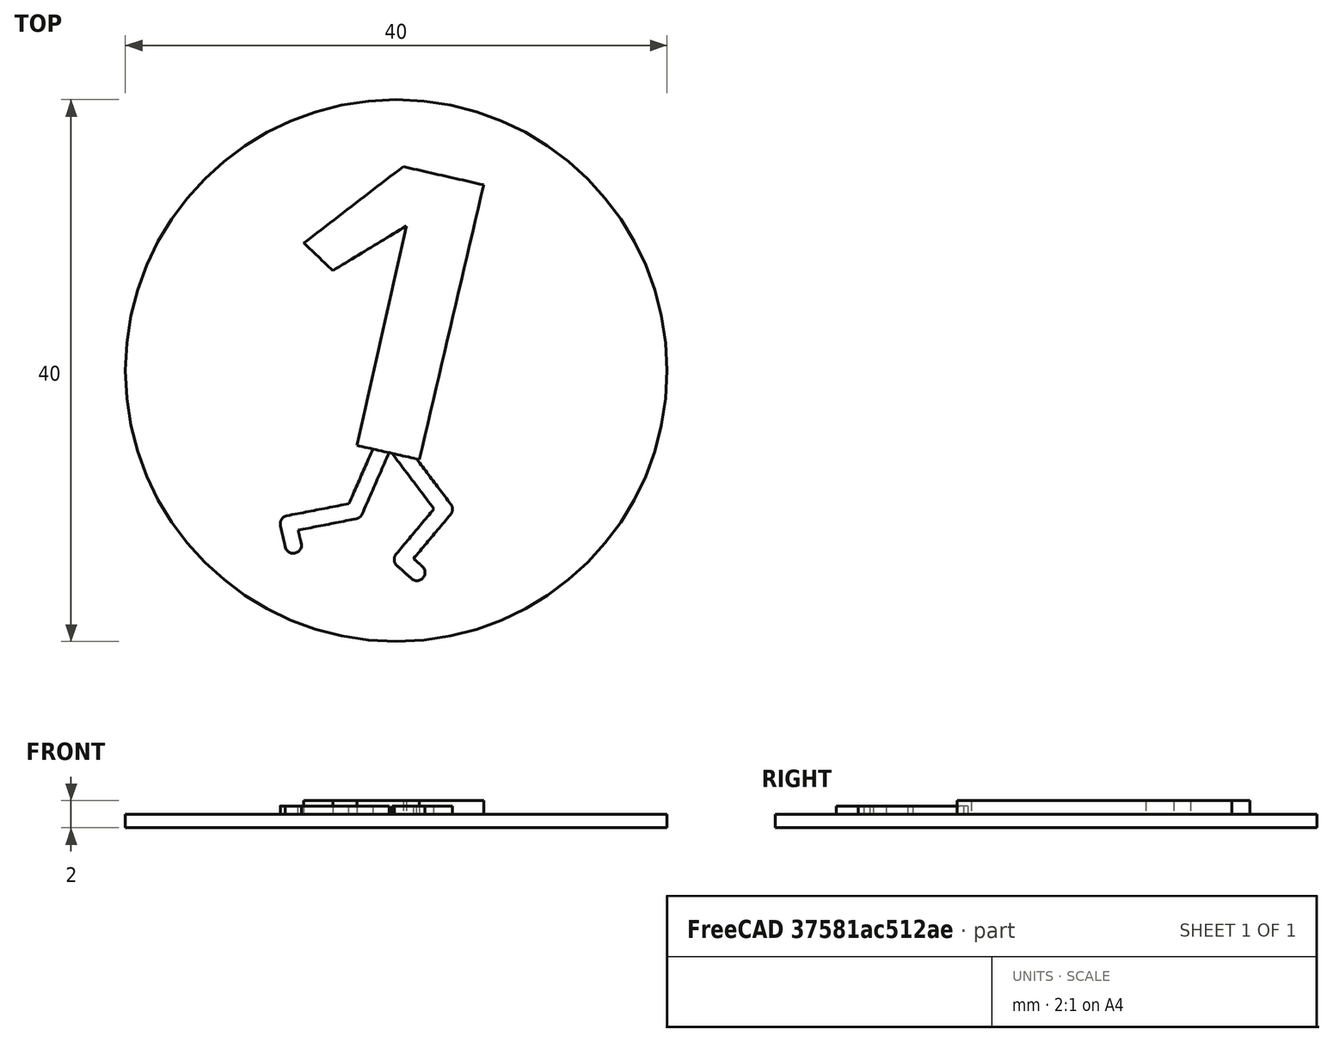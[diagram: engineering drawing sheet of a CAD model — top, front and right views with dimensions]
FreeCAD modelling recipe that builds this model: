
FCSTD DOCUMENT  (FreeCAD 0.17R12412 (Git))
Label: Bit-1-moneda
License: All rights reserved
LicenseURL: http://en.wikipedia.org/wiki/All_rights_reserved
objects: Part::Feature×2, Part::Extrusion×2, Part::MultiFuse×2, Part::Cylinder×1
note: 7 computed .brp shape members not serialized (recipe doc carries the construction recipe); baked Part::Feature solids carry a one-line shape summary decoded from their .brp

FEATURE [Part::Feature] path4_7_6_1_6
  Placement = pos=(-19.6018,20.3411,1) rot=(0,0,1;0rad)
  shape: bbox 13.27 x 21.62 x 2e-07 mm, 0 faces, 0 solids (baked)
FEATURE [Part::Feature] path6_7_2_1_0_9
  Placement = pos=(-19.6018,20.3411,1) rot=(0,0,1;0rad)
  shape: bbox 12.78 x 10.69 x 2e-07 mm, 0 faces, 0 solids (baked)
FEATURE [Part::Cylinder] Cylinder  label="base"
  Angle = 360
  AttacherType = Attacher::AttachEngine3D
  Height = 1
  Radius = 20
FEATURE [Part::Extrusion] Extrude  label="Legs"
  Base = -> path6_7_2_1_0_9
  Dir = (0,0,1)
  DirMode = 2
  FaceMakerClass = Part::FaceMakerBullseye
  LengthFwd = 0.6
  LengthRev = 0
  Solid = true
  Symmetric = false
FEATURE [Part::Extrusion] Extrude001  label="Body"
  Base = -> path4_7_6_1_6
  Dir = (0,0,-1)
  DirMode = 2
  FaceMakerClass = Part::FaceMakerBullseye
  LengthFwd = 1
  LengthRev = 0
  Placement = pos=(0,0,1) rot=(0,0,1;0rad)
  Solid = true
  Symmetric = false
FEATURE [Part::MultiFuse] Fusion  label="Bit-1"
  Shapes = -> [Extrude,Extrude001]
FEATURE [Part::MultiFuse] Fusion001  label="Bit-1-coin"
  Shapes = -> [Cylinder,Fusion]
